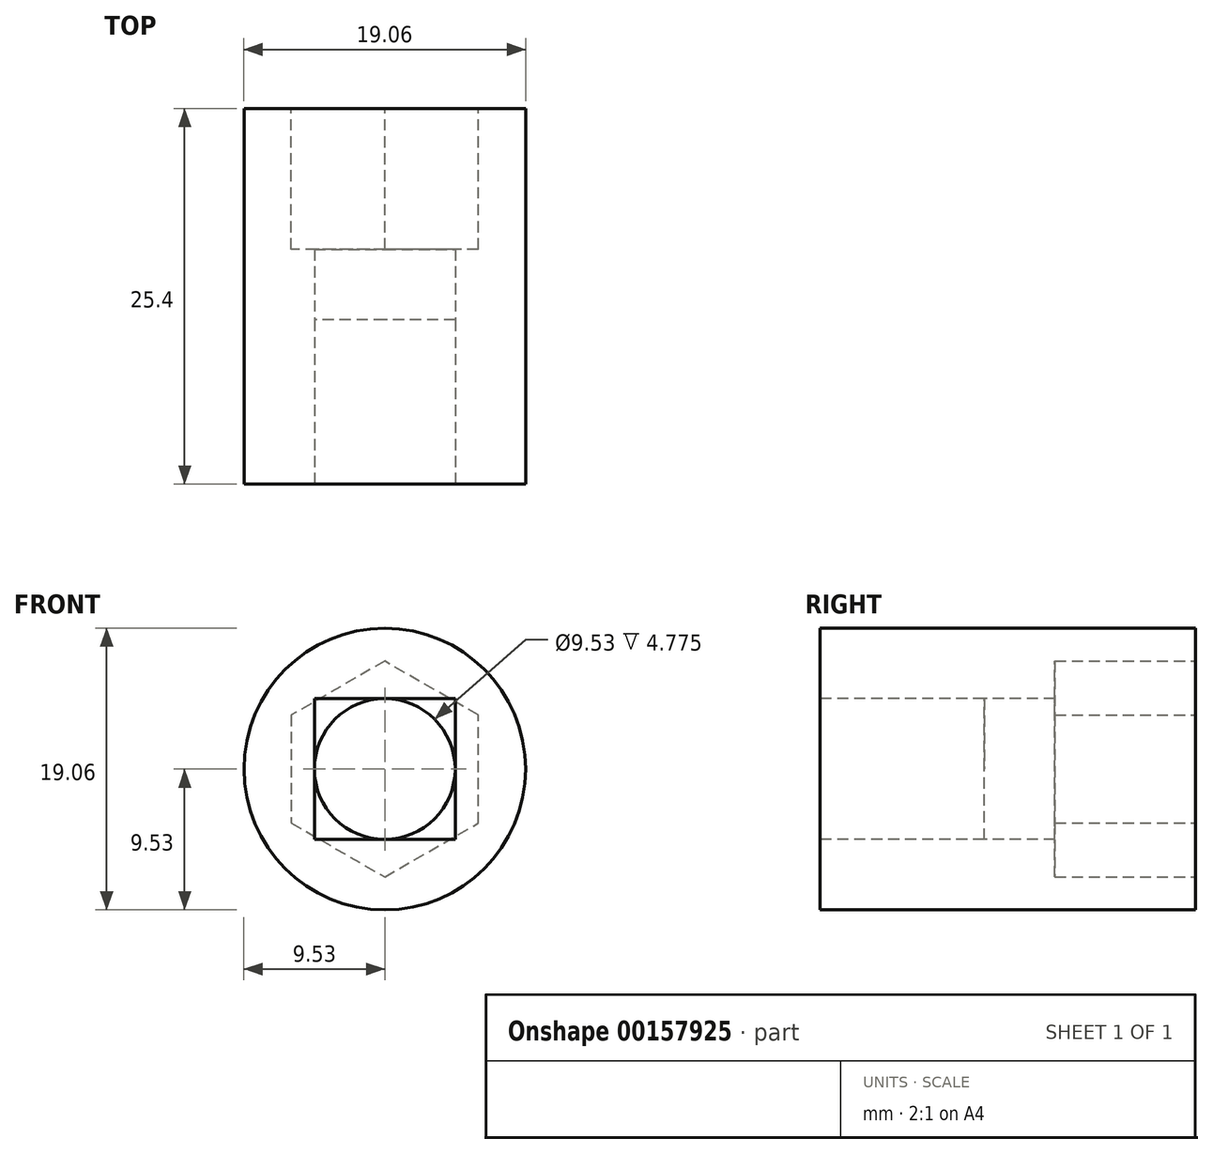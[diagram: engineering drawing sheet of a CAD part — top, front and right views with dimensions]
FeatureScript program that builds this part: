
annotation { "Feature Type Name" : "Feature", "Feature Type Description" : "" }
export const myFeature = defineFeature(function(context is Context, id is Id, definition is map)
    precondition{}
    {
        {
            var Q0;
            Q0=qCreatedBy(makeId("Front.planeOp"),FACE);
            var sketch = newSketch(context, id + "F0", { "sketchPlane" : qUnion([Q0])});
            skCircle(sketch, "E0", {"center": v(0, 0) * mm, "radius": 9.53 * mm});
            skSolve(sketch);
        }
        {
            var Q0;
            Q0 = qSketchRegion(id + "F0", true);
            extrude(context, id + "F1", {"entities" : qUnion([Q0]), "depth" : 25.4 * mm});
        }
        {
            var Q0;
            Q0=makeQuery(id+"F1.opExtrude","CAP_FACE",FACE,{"disambiguationData":[OSD([sQuery(id+"F0.wireOp",EDGE,"E0")])],"isStart":false});
            var sketch = newSketch(context, id + "F2", { "sketchPlane" : qUnion([Q0])});
            skLineSegment(sketch, "E1.bottom", {"start": v(4.76, -4.76) * mm, "end": v(-4.76, -4.76) * mm});
            skLineSegment(sketch, "E1.top", {"start": v(4.76, 4.76) * mm, "end": v(-4.76, 4.76) * mm});
            skLineSegment(sketch, "E1.left", {"start": v(4.76, -4.76) * mm, "end": v(4.76, 4.76) * mm});
            skLineSegment(sketch, "E1.right", {"start": v(-4.76, -4.76) * mm, "end": v(-4.76, 4.76) * mm});
            skPoint(sketch, "E1.middle", {"position": v(0, 0) * mm});
            skCircle(sketch, "E2", {"center": v(0, 0) * mm, "radius": 4.76 * mm});
            skSolve(sketch);
        }
        {
            var Q0;
            {var subQ0=sQuery(id+"F2.wireOp",EDGE,"E2");var subQ1=makeQuery(id+"F2.imprint","INTERSECT",VERTEX,{"derivedFrom":[sQuery(id+"F2.wireOp",EDGE,"E1.top"),subQ0]});Q0=makeQuery(id+"F2.imprint","IMPRINT",FACE,{"disambiguationData":[TD([[makeQuery(id+"F2.imprint","IMPRINT",EDGE,{"disambiguationData":[TD([[subQ1,1.0]])],"derivedFrom":subQ0}),1.0]])]});}
            var Q1;
            Q1=sQuery(id+"F2.wireOp",EDGE,"E2");
            extrude(context, id + "F3", {"entities" : qUnion([Q0]), "operationType" : NewBodyOperationType.REMOVE, "surfaceEntities" : qUnion([Q1]), "endBound" : BoundingType.THROUGH_ALL, "oppositeDirection" : true, "depth" : 25 * mm});
        }
        {
            var Q0;
            Q0 = qSketchRegion(id + "F2", true);
            extrude(context, id + "F4", {"entities" : qUnion([Q0]), "operationType" : NewBodyOperationType.REMOVE, "oppositeDirection" : true, "depth" : 11.1 * mm});
        }
        {
            var Q0;
            Q0=makeQuery(id+"F1.opExtrude","CAP_FACE",FACE,{"disambiguationData":[OSD([sQuery(id+"F0.wireOp",EDGE,"E0")])],"isStart":true});
            var sketch = newSketch(context, id + "F5", { "sketchPlane" : qUnion([Q0])});
            skCircle(sketch, "E3.cCircle", {"center": v(0, 0) * mm, "radius": 6.32 * mm, "construction": true});
            skLineSegment(sketch, "E3.0", {"start": v(6.32, 3.65) * mm, "end": v(6.32, -3.65) * mm});
            skLineSegment(sketch, "E3.1", {"start": v(6.32, -3.65) * mm, "end": v(0, -7.3) * mm});
            skLineSegment(sketch, "E3.2", {"start": v(0, -7.3) * mm, "end": v(-6.32, -3.65) * mm});
            skLineSegment(sketch, "E3.3", {"start": v(-6.32, -3.65) * mm, "end": v(-6.32, 3.65) * mm});
            skLineSegment(sketch, "E3.4", {"start": v(-6.32, 3.65) * mm, "end": v(0, 7.3) * mm});
            skLineSegment(sketch, "E3.5", {"start": v(0, 7.3) * mm, "end": v(6.32, 3.65) * mm});
            skPoint(sketch, "E3.0.midPoint", {"position": v(6.32, 0) * mm});
            skSolve(sketch);
        }
        {
            var Q0;
            Q0=makeQuery(id+"F5.imprint","IMPRINT",FACE,{"disambiguationData":[TD([[makeQuery(id+"F5.imprint","IMPRINT",EDGE,{"derivedFrom":sQuery(id+"F5.wireOp",EDGE,"E3.0")}),-1.0]])]});
            extrude(context, id + "F6", {"entities" : qUnion([Q0]), "operationType" : NewBodyOperationType.REMOVE, "oppositeDirection" : true, "depth" : 9.53 * mm});
        }
    });
